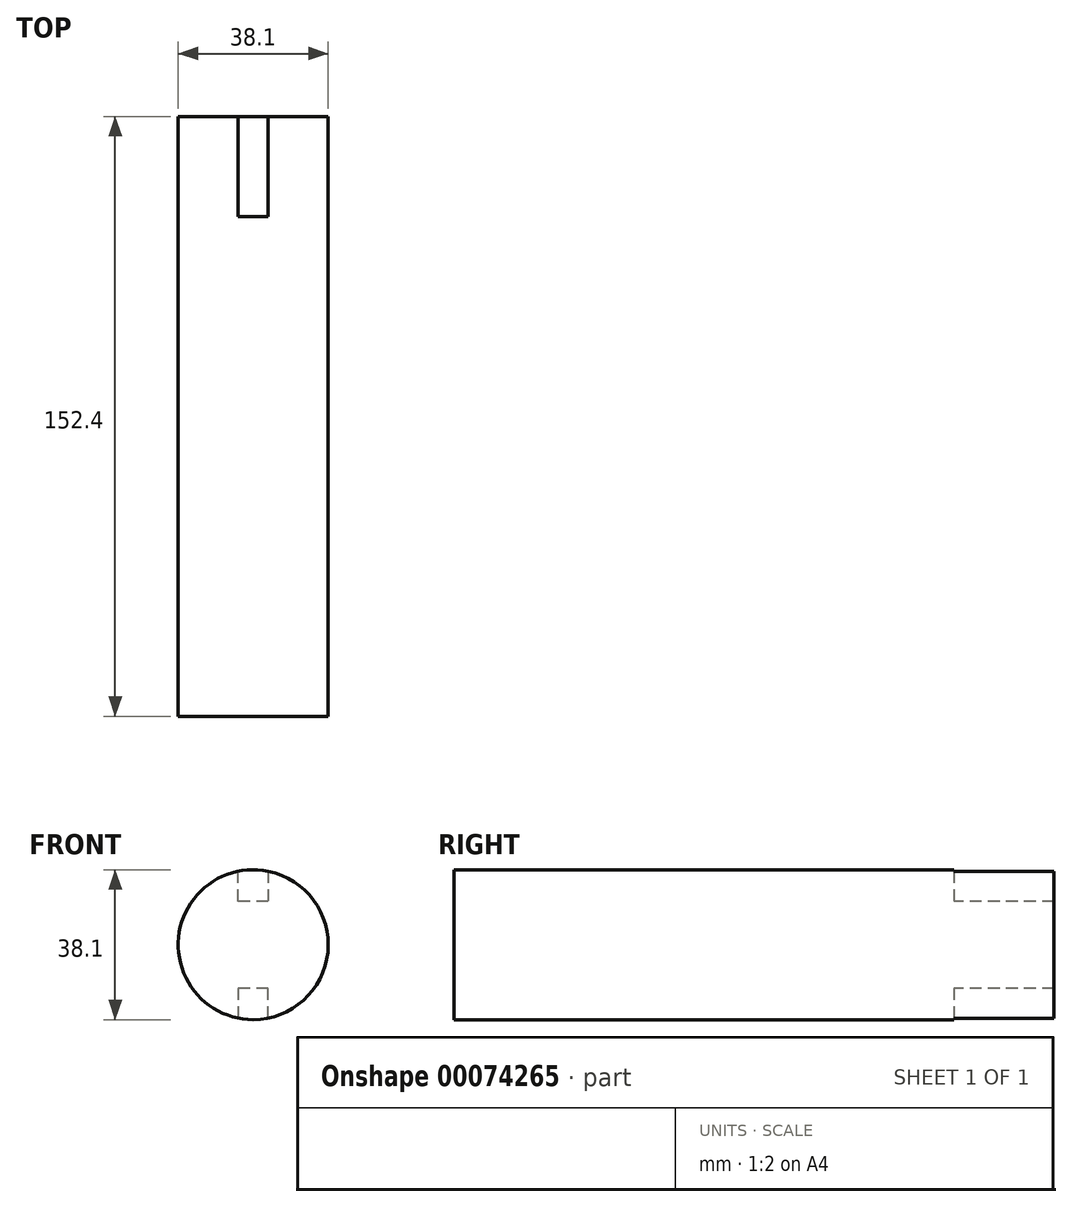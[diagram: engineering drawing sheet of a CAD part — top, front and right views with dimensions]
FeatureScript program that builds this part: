
annotation { "Feature Type Name" : "Feature", "Feature Type Description" : "" }
export const myFeature = defineFeature(function(context is Context, id is Id, definition is map)
    precondition{}
    {
        {
            var Q0;
            Q0=qCreatedBy(makeId("Front.planeOp"),FACE);
            var sketch = newSketch(context, id + "F0", { "sketchPlane" : qUnion([Q0])});
            skCircle(sketch, "E0", {"center": v(0, 0) * mm, "radius": 19.05 * mm});
            skSolve(sketch);
        }
        {
            var Q0;
            Q0 = qSketchRegion(id + "F0", true);
            extrude(context, id + "F1", {"entities" : qUnion([Q0]), "depth" : 127 * mm});
        }
        {
            var Q0;
            Q0=makeQuery(id+"F1.opExtrude","CAP_FACE",FACE,{"disambiguationData":[OSD([sQuery(id+"F0.wireOp",EDGE,"E0")])],"isStart":true});
            var sketch = newSketch(context, id + "F2", { "sketchPlane" : qUnion([Q0])});
            skLineSegment(sketch, "E1", {"start": v(-3.81, 18.67) * mm, "end": v(-3.81, 11.05) * mm});
            skLineSegment(sketch, "E2", {"start": v(-3.81, 11.05) * mm, "end": v(3.8, 11.05) * mm});
            skLineSegment(sketch, "E3", {"start": v(3.8, 11.05) * mm, "end": v(3.8, 18.67) * mm});
            skLineSegment(sketch, "E4", {"start": v(-3.81, -18.67) * mm, "end": v(-3.81, -11.05) * mm});
            skLineSegment(sketch, "E5", {"start": v(-3.81, -11.05) * mm, "end": v(3.8, -11.05) * mm});
            skLineSegment(sketch, "E6", {"start": v(3.8, -11.05) * mm, "end": v(3.8, -18.67) * mm});
            skSolve(sketch);
        }
        {
            var Q0;
            {var subQ2=sQuery(id+"F2.wireOp",EDGE,"E1");Q0=makeQuery(id+"F2.imprint","IMPRINT",FACE,{"disambiguationData":[TD([[makeQuery(id+"F2.imprint","IMPRINT",EDGE,{"derivedFrom":subQ2}),-1.0]])]});}
            extrude(context, id + "F3", {"entities" : qUnion([Q0]), "operationType" : NewBodyOperationType.ADD, "depth" : 25.4 * mm});
        }
    });
